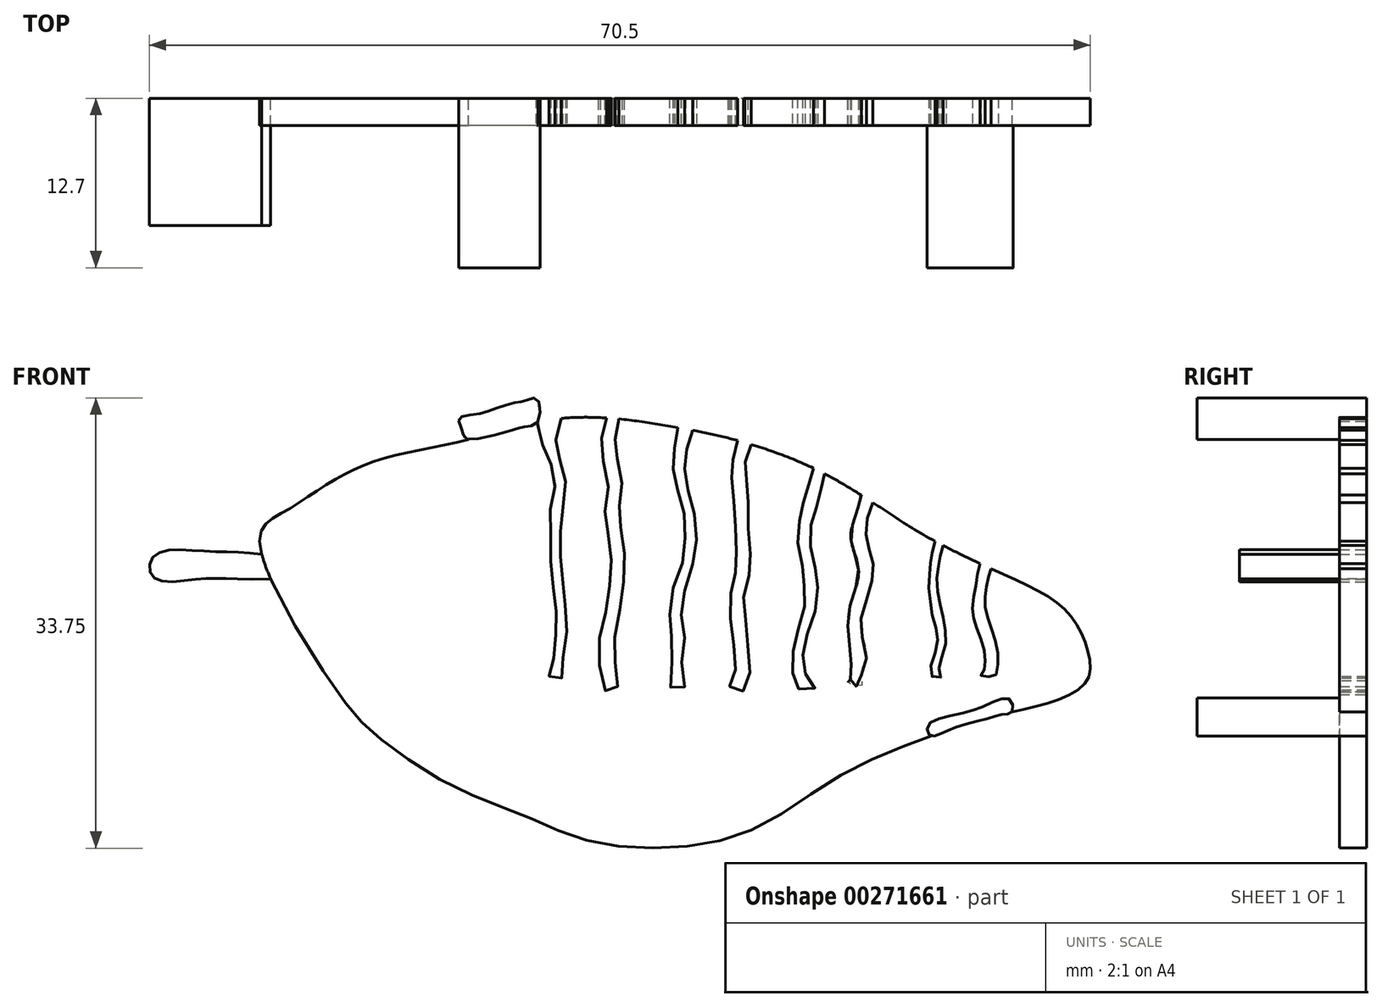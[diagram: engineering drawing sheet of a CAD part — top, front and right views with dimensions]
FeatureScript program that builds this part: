
annotation { "Feature Type Name" : "Feature", "Feature Type Description" : "" }
export const myFeature = defineFeature(function(context is Context, id is Id, definition is map)
    precondition{}
    {
        {
            var Q0;
            Q0=qCreatedBy(makeId("Front.planeOp"),FACE);
            var sketch = newSketch(context, id + "F0", { "sketchPlane" : qUnion([Q0])});
            skFitSpline(sketch, "E0", {"points": [v(-28.45, 9.74) * mm, v(-24.57, 11.38) * mm, v(-19.05, 12.59) * mm, v(-14.06, 13.95) * mm, v(-8.84, 14.4) * mm, v(-3.18, 13.72) * mm, v(2.04, 12.59) * mm, v(7.03, 10.77) * mm, v(11.11, 8.5) * mm, v(16.03, 5.4) * mm, v(22.22, 2.38) * mm, v(26.26, 0) * mm, v(27.9, -2.83) * mm, v(27.9, -5.33) * mm, v(24.5, -7.15) * mm, v(19.73, -8.28) * mm, v(15.38, -9.8) * mm, v(9.52, -12.36) * mm, v(3.4, -16.22) * mm, v(-2.72, -17.8) * mm, v(-9.3, -17.35) * mm, v(-14.06, -15.53) * mm, v(-19.96, -13.04) * mm, v(-25.63, -9.18) * mm, v(-28.34, -6.02) * mm, v(-34.06, 5.34) * mm, v(-32.06, 7.44) * mm, v(-28.45, 9.74) * mm]});
            skFitSpline(sketch, "E1", {"points": [v(-33.9, 4.15) * mm, v(-38.31, 4.39) * mm, v(-41.98, 4.03) * mm, v(-42.01, 2.4) * mm, v(-38.5, 2.3) * mm, v(-33.24, 2.3) * mm], "startDerivative": vector(-21.58, 2.71) * mm, "endDerivative": vector(36.33, 1.24) * mm});
            skSolve(sketch);
        }
        {
            var Q0;
            Q0=makeQuery(id+"F0.imprint","IMPRINT",FACE,{"disambiguationData":[TD([[makeQuery(id+"F0.imprint","IMPRINT",EDGE,{"derivedFrom":sQuery(id+"F0.wireOp",EDGE,"E0")}),-1.0]])]});
            extrude(context, id + "F1", {"entities" : qUnion([Q0]), "depth" : 2.03 * mm});
        }
        {
            var Q0;
            Q0=makeQuery(id+"F1.opExtrude","CAP_FACE",FACE,{"disambiguationData":[OSD([sQuery(id+"F0.wireOp",EDGE,"E0")])],"isStart":false});
            var sketch = newSketch(context, id + "F2", { "sketchPlane" : qUnion([Q0])});
            skSolve(sketch);
        }
        {
            var Q0;
            {var subQ0=sQuery(id+"F0.wireOp",EDGE,"E1");Q0=makeQuery(id+"F0.imprint","IMPRINT",FACE,{"disambiguationData":[TD([[makeQuery(id+"F0.imprint","IMPRINT",EDGE,{"derivedFrom":subQ0}),1.0]])]});}
            extrude(context, id + "F3", {"entities" : qUnion([Q0]), "operationType" : NewBodyOperationType.ADD, "depth" : 9.52 * mm});
        }
        {
            var Q0;
            Q0=qCreatedBy(makeId("Front.planeOp"),FACE);
            var sketch = newSketch(context, id + "F4", { "sketchPlane" : qUnion([Q0])});
            skFitSpline(sketch, "E2", {"points": [v(-13.25, 14.05) * mm, v(-14.17, 13.72) * mm, v(-14.97, 13.51) * mm, v(-18.6, 12.79) * mm, v(-18.88, 13.42) * mm, v(-19.13, 14.32) * mm, v(-17.83, 14.64) * mm, v(-16.4, 15.06) * mm, v(-14.82, 15.53) * mm, v(-14.13, 15.67) * mm, v(-13.29, 15.8) * mm, v(-13.25, 14.05) * mm]});
            skFitSpline(sketch, "E3", {"points": [v(22.33, -7.64) * mm, v(22.1, -6.7) * mm, v(20.53, -7.09) * mm, v(18.1, -7.87) * mm, v(16, -8.65) * mm, v(16.15, -9.44) * mm, v(17, -9.3) * mm, v(18.34, -8.73) * mm, v(20.75, -8.1) * mm, v(21.67, -7.85) * mm, v(22.33, -7.64) * mm]});
            skSolve(sketch);
        }
        {
            var Q0;
            Q0=makeQuery(id+"F4.imprint","IMPRINT",FACE,{"disambiguationData":[TD([[makeQuery(id+"F4.imprint","IMPRINT",EDGE,{"derivedFrom":sQuery(id+"F4.wireOp",EDGE,"E2")}),-1.0]])]});
            var Q1;
            Q1=makeQuery(id+"F4.imprint","IMPRINT",FACE,{"disambiguationData":[TD([[makeQuery(id+"F4.imprint","IMPRINT",EDGE,{"derivedFrom":sQuery(id+"F4.wireOp",EDGE,"E3")}),1.0]])]});
            extrude(context, id + "F5", {"entities" : qUnion([Q0, Q1]), "operationType" : NewBodyOperationType.ADD, "depth" : 12.7 * mm});
        }
        {
            var Q0;
            Q0=makeQuery(id+"F1.opExtrude","CAP_FACE",FACE,{"disambiguationData":[OSD([sQuery(id+"F0.wireOp",EDGE,"E0")])],"isStart":false});
            var sketch = newSketch(context, id + "F6", { "sketchPlane" : qUnion([Q0])});
            skFitSpline(sketch, "E4", {"points": [v(-13.21, 14.11) * mm, v(-12.97, 12.54) * mm, v(-12.35, 11.13) * mm, v(-11.91, 9.55) * mm, v(-12.26, 7.8) * mm, v(-12.26, 5.68) * mm, v(-12.26, 3.4) * mm, v(-12, 1.2) * mm, v(-11.83, -0.65) * mm, v(-11.91, -2.5) * mm, v(-12.18, -4.26) * mm, v(-12.35, -5.05) * mm, v(-11.54, -5.31) * mm, v(-11.46, -4.37) * mm, v(-11.13, -2.67) * mm, v(-11.15, 0) * mm, v(-11.29, 1.38) * mm, v(-11.5, 3.66) * mm, v(-11.55, 5.77) * mm, v(-11.33, 7.75) * mm, v(-11.18, 9.9) * mm, v(-11.7, 11.5) * mm, v(-11.9, 12.7) * mm, v(-11.46, 14.34) * mm, v(-13.21, 14.11) * mm]});
            skFitSpline(sketch, "E5", {"points": [v(-7.17, 14.29) * mm, v(-7.34, 13.33) * mm, v(-7.43, 12.45) * mm, v(-7.34, 11.66) * mm, v(-7.08, 10.52) * mm, v(-6.9, 9.02) * mm, v(-7.08, 7.88) * mm, v(-7.25, 7.09) * mm, v(-6.9, 5.77) * mm, v(-6.73, 4.18) * mm, v(-6.81, 2.34) * mm, v(-6.9, 0.76) * mm, v(-7.43, -1.35) * mm, v(-7.43, -2.59) * mm, v(-7.43, -4.08) * mm, v(-7.25, -5.4) * mm, v(-7.43, -6.28) * mm, v(-8.09, -6.2) * mm, v(-8.52, -4.78) * mm, v(-8.68, -3.37) * mm, v(-8.53, -1.57) * mm, v(-8.09, -0.04) * mm, v(-7.87, 1.54) * mm, v(-7.78, 3.04) * mm, v(-7.74, 4.45) * mm, v(-8.09, 6.25) * mm, v(-8.2, 7.09) * mm, v(-8.09, 8.26) * mm, v(-7.95, 9.72) * mm, v(-8.34, 11.24) * mm, v(-8.5, 12.36) * mm, v(-8.31, 13.66) * mm, v(-8.09, 14.36) * mm, v(-7.17, 14.29) * mm]});
            skFitSpline(sketch, "E6", {"points": [v(-2.74, 13.64) * mm, v(-2.97, 12.63) * mm, v(-3.06, 11.57) * mm, v(-3.08, 10.51) * mm, v(-2.95, 9.72) * mm, v(-2.56, 8.32) * mm, v(-2.24, 6.9) * mm, v(-2.2, 5.42) * mm, v(-2.22, 4) * mm, v(-2.88, 2.47) * mm, v(-3.19, 0.79) * mm, v(-3.36, -0.83) * mm, v(-3.24, -1.89) * mm, v(-3.13, -3.37) * mm, v(-3.37, -5.06) * mm, v(-3.04, -6.12) * mm, v(-2.27, -6) * mm, v(-2.48, -4.78) * mm, v(-2.33, -3.33) * mm, v(-2.24, -1.84) * mm, v(-2.45, -0.64) * mm, v(-2.44, 0.64) * mm, v(-1.92, 2.37) * mm, v(-1.5, 4.02) * mm, v(-1.34, 5.4) * mm, v(-1.47, 7.02) * mm, v(-1.83, 8.43) * mm, v(-2.13, 9.72) * mm, v(-2.22, 10.71) * mm, v(-2.13, 11.69) * mm, v(-1.94, 12.46) * mm, v(-1.62, 13.44) * mm, v(-2.74, 13.64) * mm]});
            skFitSpline(sketch, "E7", {"points": [v(2.76, 12.38) * mm, v(2.39, 11.3) * mm, v(2.3, 10.32) * mm, v(2.48, 9.04) * mm, v(2.52, 7.07) * mm, v(2.61, 4.81) * mm, v(2.72, 3.12) * mm, v(2.28, 1.58) * mm, v(2.24, 0) * mm, v(2.49, -2.02) * mm, v(2.58, -4.28) * mm, v(2.48, -5.97) * mm, v(1.07, -6) * mm, v(1.38, -5.46) * mm, v(1.58, -4.33) * mm, v(1.4, -2.2) * mm, v(1.15, 0) * mm, v(1.38, 1.9) * mm, v(1.62, 3.15) * mm, v(1.64, 4.77) * mm, v(1.54, 6.89) * mm, v(1.4, 8.92) * mm, v(1.28, 10.4) * mm, v(1.4, 11.45) * mm, v(1.74, 12.67) * mm, v(2.76, 12.38) * mm]});
            skFitSpline(sketch, "E8", {"points": [v(7.44, 10.58) * mm, v(7.16, 9.82) * mm, v(6.9, 8.85) * mm, v(6.58, 7.68) * mm, v(6.37, 6.66) * mm, v(6.22, 5.18) * mm, v(6.56, 3.43) * mm, v(6.68, 2.18) * mm, v(6.8, 1.03) * mm, v(6.55, -0.63) * mm, v(6.05, -2.18) * mm, v(5.85, -3.75) * mm, v(5.91, -5.14) * mm, v(6.26, -5.9) * mm, v(7.1, -6.01) * mm, v(7.6, -5.77) * mm, v(6.83, -4.8) * mm, v(6.6, -3.74) * mm, v(6.77, -2.45) * mm, v(7.32, -0.86) * mm, v(7.74, 1.02) * mm, v(7.66, 2.4) * mm, v(7.44, 3.59) * mm, v(7.17, 5.14) * mm, v(7.26, 6.5) * mm, v(7.58, 7.5) * mm, v(7.94, 8.69) * mm, v(8.13, 9.56) * mm, v(8.25, 10.18) * mm, v(7.44, 10.58) * mm]});
            skFitSpline(sketch, "E9", {"points": [v(11.86, 8.02) * mm, v(11.5, 7.01) * mm, v(11.38, 6.03) * mm, v(11.41, 5.04) * mm, v(11.67, 4.33) * mm, v(11.9, 3.32) * mm, v(11.84, 2.34) * mm, v(11.45, 0.88) * mm, v(11, -0.6) * mm, v(11, -1.82) * mm, v(11.41, -3.57) * mm, v(11, -4.7) * mm, v(11, -5.7) * mm, v(10.02, -5.52) * mm, v(10.15, -5.27) * mm, v(10.26, -4.69) * mm, v(10.2, -3.25) * mm, v(10.04, -1.9) * mm, v(10.02, -0.42) * mm, v(10.41, 1.15) * mm, v(10.78, 2.45) * mm, v(10.74, 3.4) * mm, v(10.5, 4.22) * mm, v(10.27, 5.01) * mm, v(10.24, 5.9) * mm, v(10.58, 7.12) * mm, v(10.9, 8.14) * mm, v(11, 8.57) * mm, v(11.47, 8.36) * mm, v(11.86, 8.02) * mm]});
            skFitSpline(sketch, "E10", {"points": [v(16.55, 5.12) * mm, v(16.33, 4.38) * mm, v(16.18, 3.63) * mm, v(16.17, 3.1) * mm, v(16.06, 2.09) * mm, v(16.14, 0.96) * mm, v(16.23, 0) * mm, v(16.5, -1.09) * mm, v(16.69, -1.96) * mm, v(16.66, -2.85) * mm, v(16.3, -3.9) * mm, v(16.2, -4.74) * mm, v(16.49, -5.15) * mm, v(16.96, -5.05) * mm, v(16.84, -4.6) * mm, v(16.88, -4) * mm, v(17.26, -2.98) * mm, v(17.34, -1.98) * mm, v(17.2, -1) * mm, v(16.99, 0) * mm, v(16.78, 0.97) * mm, v(16.67, 2.08) * mm, v(16.73, 2.99) * mm, v(16.84, 3.63) * mm, v(16.97, 4.23) * mm, v(17.13, 4.85) * mm, v(16.82, 5.02) * mm, v(16.55, 5.12) * mm]});
            skFitSpline(sketch, "E11", {"points": [v(20.72, 3.07) * mm, v(20.53, 2.44) * mm, v(20.37, 1.5) * mm, v(20.28, 0.68) * mm, v(20.38, -0.3) * mm, v(20.76, -1.48) * mm, v(21.18, -2.9) * mm, v(21.24, -4.11) * mm, v(21.04, -4.93) * mm, v(20.45, -5.04) * mm, v(19.97, -4.95) * mm, v(20.18, -4.6) * mm, v(20.3, -4.02) * mm, v(20.2, -3) * mm, v(19.82, -1.82) * mm, v(19.46, -0.78) * mm, v(19.34, 0) * mm, v(19.47, 1.28) * mm, v(19.68, 2.29) * mm, v(19.89, 3.45) * mm, v(20.32, 3.25) * mm, v(20.72, 3.07) * mm]});
            skSolve(sketch);
        }
        {
            var Q0;
            {var subQ0=sQuery(id+"F6.wireOp",EDGE,"E5");var subQ1=sQuery(id+"F0.wireOp",EDGE,"E0");var subQ2=makeQuery(id+"F1.opExtrude","SWEPT_FACE",FACE,{"disambiguationData":[OSD([subQ1])]});var subQ3=makeQuery(id+"F1.opExtrude","CAP_FACE",FACE,{"disambiguationData":[OSD([subQ1])],"isStart":false});var subQ4=makeQuery(id+"FEO1aFnhTrQs56K_1.opExtrude","SWEPT_FACE",FACE,{"disambiguationData":[OSD([sQuery(id+"F2.wireOp",EDGE,"58dd70b2-1d15-4010-9a82-05c4c9745bfd")])]});var subQ5=makeQuery(id+"FEO1aFnhTrQs56K_1.boolean.opBoolean","COPY",FACE,{"derivedFrom":subQ4});var subQ6=makeQuery(id+"F5.boolean.opBoolean","SPLIT",EDGE,{"disambiguationData":[TD([subQ5])],"derivedFrom":makeQuery(id+"F3.boolean.opBoolean","SPLIT",EDGE,{"disambiguationData":[TD([subQ2,subQ3,subQ5,makeQuery(id+"F3.opExtrude","SWEPT_FACE",FACE,{"disambiguationData":[OSD([subQ1])]}),makeQuery(id+"F3.opExtrude","SWEPT_FACE",FACE,{"disambiguationData":[OSD([sQuery(id+"F0.wireOp",EDGE,"E1")])]})])],"derivedFrom":makeQuery(id+"FEO1aFnhTrQs56K_1.boolean.opBoolean","SPLIT",EDGE,{"disambiguationData":[TD([subQ2,subQ3,subQ4,makeQuery(id+"FEO1aFnhTrQs56K_1.opExtrude","SWEPT_FACE",FACE,{"disambiguationData":[OSD([sQuery(id+"F2.wireOp",EDGE,"c8b85a6c-cabf-4dfb-9f84-1d43b1ba4017")])]})])],"derivedFrom":makeQuery(id+"F1.opExtrude","CAP_EDGE",EDGE,{"disambiguationData":[OSD([subQ1])],"isStart":false})})})});var subQ7=makeQuery(id+"F6.imprint","INTERSECT",VERTEX,{"disambiguationData":[OD(0.0)],"derivedFrom":[subQ6,subQ0]});Q0=makeQuery(id+"F6.imprint","IMPRINT",FACE,{"disambiguationData":[TD([[makeQuery(id+"F6.imprint","IMPRINT",EDGE,{"disambiguationData":[TD([[subQ7,-1.0]])],"derivedFrom":subQ0}),-1.0]])]});}
            var Q1;
            {var subQ0=sQuery(id+"F6.wireOp",EDGE,"E4");var subQ1=makeQuery(id+"F5.opExtrude","SWEPT_FACE",FACE,{"disambiguationData":[OSD([sQuery(id+"F4.wireOp",EDGE,"E2")])]});var subQ2=sQuery(id+"F0.wireOp",EDGE,"E0");var subQ3=makeQuery(id+"F1.opExtrude","CAP_FACE",FACE,{"disambiguationData":[OSD([subQ2])],"isStart":false});var subQ4=makeQuery(id+"F5.boolean.opBoolean","INTERSECT",EDGE,{"derivedFrom":[subQ3,subQ1]});var subQ5=makeQuery(id+"F6.imprint","INTERSECT",VERTEX,{"derivedFrom":[subQ4,subQ0]});Q1=makeQuery(id+"F6.imprint","IMPRINT",FACE,{"disambiguationData":[TD([[makeQuery(id+"F6.imprint","IMPRINT",EDGE,{"disambiguationData":[TD([[subQ5,-1.0]])],"derivedFrom":subQ0}),1.0]])]});}
            var Q2;
            {var subQ0=sQuery(id+"F6.wireOp",EDGE,"E4");var subQ1=makeQuery(id+"F5.opExtrude","SWEPT_FACE",FACE,{"disambiguationData":[OSD([sQuery(id+"F4.wireOp",EDGE,"E2")])]});var subQ2=sQuery(id+"F0.wireOp",EDGE,"E0");var subQ3=makeQuery(id+"F1.opExtrude","CAP_FACE",FACE,{"disambiguationData":[OSD([subQ2])],"isStart":false});var subQ4=makeQuery(id+"F5.boolean.opBoolean","INTERSECT",EDGE,{"derivedFrom":[subQ3,subQ1]});var subQ5=makeQuery(id+"F6.imprint","INTERSECT",VERTEX,{"disambiguationData":[OD(0.0)],"derivedFrom":[subQ4,subQ0]});Q2=makeQuery(id+"F6.imprint","IMPRINT",FACE,{"disambiguationData":[TD([[makeQuery(id+"F6.imprint","IMPRINT",EDGE,{"disambiguationData":[TD([[subQ5,-1.0]])],"derivedFrom":subQ4}),-1.0]])]});}
            var Q3;
            {var subQ0=sQuery(id+"F6.wireOp",EDGE,"E5");var subQ1=sQuery(id+"F0.wireOp",EDGE,"E0");var subQ2=makeQuery(id+"F5.boolean.opBoolean","SPLIT",EDGE,{"disambiguationData":[TD([makeQuery(id+"F1.opExtrude","SWEPT_FACE",FACE,{"disambiguationData":[OSD([subQ1])]}),makeQuery(id+"F1.opExtrude","CAP_FACE",FACE,{"disambiguationData":[OSD([subQ1])],"isStart":false}),makeQuery(id+"F5.opExtrude","SWEPT_FACE",FACE,{"disambiguationData":[OSD([sQuery(id+"F4.wireOp",EDGE,"E2")])]}),makeQuery(id+"F5.opExtrude","SWEPT_FACE",FACE,{"disambiguationData":[OSD([sQuery(id+"F4.wireOp",EDGE,"E3")])]})])],"derivedFrom":makeQuery(id+"F3.boolean.opBoolean","SPLIT",EDGE,{"disambiguationData":[OD(0.0)],"derivedFrom":makeQuery(id+"F1.opExtrude","CAP_EDGE",EDGE,{"disambiguationData":[OSD([subQ1])],"isStart":false})})});var subQ3=makeQuery(id+"F6.imprint","INTERSECT",VERTEX,{"disambiguationData":[OD(0.0)],"derivedFrom":[subQ2,subQ0]});Q3=makeQuery(id+"F6.imprint","IMPRINT",FACE,{"disambiguationData":[TD([[makeQuery(id+"F6.imprint","IMPRINT",EDGE,{"disambiguationData":[TD([[subQ3,1.0]])],"derivedFrom":subQ0}),-1.0]])]});}
            var Q4;
            {var subQ0=sQuery(id+"F6.wireOp",EDGE,"E6");var subQ1=sQuery(id+"F0.wireOp",EDGE,"E0");var subQ2=makeQuery(id+"F5.boolean.opBoolean","SPLIT",EDGE,{"disambiguationData":[TD([makeQuery(id+"F1.opExtrude","SWEPT_FACE",FACE,{"disambiguationData":[OSD([subQ1])]}),makeQuery(id+"F1.opExtrude","CAP_FACE",FACE,{"disambiguationData":[OSD([subQ1])],"isStart":false}),makeQuery(id+"F5.opExtrude","SWEPT_FACE",FACE,{"disambiguationData":[OSD([sQuery(id+"F4.wireOp",EDGE,"E2")])]}),makeQuery(id+"F5.opExtrude","SWEPT_FACE",FACE,{"disambiguationData":[OSD([sQuery(id+"F4.wireOp",EDGE,"E3")])]})])],"derivedFrom":makeQuery(id+"F3.boolean.opBoolean","SPLIT",EDGE,{"disambiguationData":[OD(0.0)],"derivedFrom":makeQuery(id+"F1.opExtrude","CAP_EDGE",EDGE,{"disambiguationData":[OSD([subQ1])],"isStart":false})})});var subQ3=makeQuery(id+"F6.imprint","INTERSECT",VERTEX,{"disambiguationData":[OD(0.0)],"derivedFrom":[subQ2,subQ0]});Q4=makeQuery(id+"F6.imprint","IMPRINT",FACE,{"disambiguationData":[TD([[makeQuery(id+"F6.imprint","IMPRINT",EDGE,{"disambiguationData":[TD([[subQ3,-1.0]])],"derivedFrom":subQ0}),1.0]])]});}
            var Q5;
            {var subQ0=sQuery(id+"F6.wireOp",EDGE,"E7");var subQ1=sQuery(id+"F0.wireOp",EDGE,"E0");var subQ2=makeQuery(id+"F5.boolean.opBoolean","SPLIT",EDGE,{"disambiguationData":[TD([makeQuery(id+"F1.opExtrude","SWEPT_FACE",FACE,{"disambiguationData":[OSD([subQ1])]}),makeQuery(id+"F1.opExtrude","CAP_FACE",FACE,{"disambiguationData":[OSD([subQ1])],"isStart":false}),makeQuery(id+"F5.opExtrude","SWEPT_FACE",FACE,{"disambiguationData":[OSD([sQuery(id+"F4.wireOp",EDGE,"E2")])]}),makeQuery(id+"F5.opExtrude","SWEPT_FACE",FACE,{"disambiguationData":[OSD([sQuery(id+"F4.wireOp",EDGE,"E3")])]})])],"derivedFrom":makeQuery(id+"F3.boolean.opBoolean","SPLIT",EDGE,{"disambiguationData":[OD(0.0)],"derivedFrom":makeQuery(id+"F1.opExtrude","CAP_EDGE",EDGE,{"disambiguationData":[OSD([subQ1])],"isStart":false})})});var subQ3=makeQuery(id+"F6.imprint","INTERSECT",VERTEX,{"disambiguationData":[OD(0.0)],"derivedFrom":[subQ2,subQ0]});Q5=makeQuery(id+"F6.imprint","IMPRINT",FACE,{"disambiguationData":[TD([[makeQuery(id+"F6.imprint","IMPRINT",EDGE,{"disambiguationData":[TD([[subQ3,-1.0]])],"derivedFrom":subQ0}),-1.0]])]});}
            var Q6;
            {var subQ0=sQuery(id+"F6.wireOp",EDGE,"E8");var subQ1=sQuery(id+"F0.wireOp",EDGE,"E0");var subQ2=makeQuery(id+"F5.boolean.opBoolean","SPLIT",EDGE,{"disambiguationData":[TD([makeQuery(id+"F1.opExtrude","SWEPT_FACE",FACE,{"disambiguationData":[OSD([subQ1])]}),makeQuery(id+"F1.opExtrude","CAP_FACE",FACE,{"disambiguationData":[OSD([subQ1])],"isStart":false}),makeQuery(id+"F5.opExtrude","SWEPT_FACE",FACE,{"disambiguationData":[OSD([sQuery(id+"F4.wireOp",EDGE,"E2")])]}),makeQuery(id+"F5.opExtrude","SWEPT_FACE",FACE,{"disambiguationData":[OSD([sQuery(id+"F4.wireOp",EDGE,"E3")])]})])],"derivedFrom":makeQuery(id+"F3.boolean.opBoolean","SPLIT",EDGE,{"disambiguationData":[OD(0.0)],"derivedFrom":makeQuery(id+"F1.opExtrude","CAP_EDGE",EDGE,{"disambiguationData":[OSD([subQ1])],"isStart":false})})});var subQ3=makeQuery(id+"F6.imprint","INTERSECT",VERTEX,{"disambiguationData":[OD(0.0)],"derivedFrom":[subQ2,subQ0]});Q6=makeQuery(id+"F6.imprint","IMPRINT",FACE,{"disambiguationData":[TD([[makeQuery(id+"F6.imprint","IMPRINT",EDGE,{"disambiguationData":[TD([[subQ3,1.0]])],"derivedFrom":subQ0}),1.0]])]});}
            var Q7;
            {var subQ0=sQuery(id+"F6.wireOp",EDGE,"E9");var subQ1=sQuery(id+"F0.wireOp",EDGE,"E0");var subQ2=makeQuery(id+"F5.boolean.opBoolean","SPLIT",EDGE,{"disambiguationData":[TD([makeQuery(id+"F1.opExtrude","SWEPT_FACE",FACE,{"disambiguationData":[OSD([subQ1])]}),makeQuery(id+"F1.opExtrude","CAP_FACE",FACE,{"disambiguationData":[OSD([subQ1])],"isStart":false}),makeQuery(id+"F5.opExtrude","SWEPT_FACE",FACE,{"disambiguationData":[OSD([sQuery(id+"F4.wireOp",EDGE,"E2")])]}),makeQuery(id+"F5.opExtrude","SWEPT_FACE",FACE,{"disambiguationData":[OSD([sQuery(id+"F4.wireOp",EDGE,"E3")])]})])],"derivedFrom":makeQuery(id+"F3.boolean.opBoolean","SPLIT",EDGE,{"disambiguationData":[OD(0.0)],"derivedFrom":makeQuery(id+"F1.opExtrude","CAP_EDGE",EDGE,{"disambiguationData":[OSD([subQ1])],"isStart":false})})});var subQ3=makeQuery(id+"F6.imprint","INTERSECT",VERTEX,{"disambiguationData":[OD(0.0)],"derivedFrom":[subQ2,subQ0]});Q7=makeQuery(id+"F6.imprint","IMPRINT",FACE,{"disambiguationData":[TD([[makeQuery(id+"F6.imprint","IMPRINT",EDGE,{"disambiguationData":[TD([[subQ3,1.0]])],"derivedFrom":subQ0}),-1.0]])]});}
            var Q8;
            {var subQ0=sQuery(id+"F6.wireOp",EDGE,"E10");var subQ1=sQuery(id+"F0.wireOp",EDGE,"E0");var subQ2=makeQuery(id+"F5.boolean.opBoolean","SPLIT",EDGE,{"disambiguationData":[TD([makeQuery(id+"F1.opExtrude","SWEPT_FACE",FACE,{"disambiguationData":[OSD([subQ1])]}),makeQuery(id+"F1.opExtrude","CAP_FACE",FACE,{"disambiguationData":[OSD([subQ1])],"isStart":false}),makeQuery(id+"F5.opExtrude","SWEPT_FACE",FACE,{"disambiguationData":[OSD([sQuery(id+"F4.wireOp",EDGE,"E2")])]}),makeQuery(id+"F5.opExtrude","SWEPT_FACE",FACE,{"disambiguationData":[OSD([sQuery(id+"F4.wireOp",EDGE,"E3")])]})])],"derivedFrom":makeQuery(id+"F3.boolean.opBoolean","SPLIT",EDGE,{"disambiguationData":[OD(0.0)],"derivedFrom":makeQuery(id+"F1.opExtrude","CAP_EDGE",EDGE,{"disambiguationData":[OSD([subQ1])],"isStart":false})})});var subQ3=makeQuery(id+"F6.imprint","INTERSECT",VERTEX,{"disambiguationData":[OD(0.0)],"derivedFrom":[subQ2,subQ0]});Q8=makeQuery(id+"F6.imprint","IMPRINT",FACE,{"disambiguationData":[TD([[makeQuery(id+"F6.imprint","IMPRINT",EDGE,{"disambiguationData":[TD([[subQ3,-1.0]])],"derivedFrom":subQ0}),1.0]])]});}
            var Q9;
            {var subQ0=sQuery(id+"F6.wireOp",EDGE,"E11");var subQ1=sQuery(id+"F0.wireOp",EDGE,"E0");var subQ2=makeQuery(id+"F5.boolean.opBoolean","SPLIT",EDGE,{"disambiguationData":[TD([makeQuery(id+"F1.opExtrude","SWEPT_FACE",FACE,{"disambiguationData":[OSD([subQ1])]}),makeQuery(id+"F1.opExtrude","CAP_FACE",FACE,{"disambiguationData":[OSD([subQ1])],"isStart":false}),makeQuery(id+"F5.opExtrude","SWEPT_FACE",FACE,{"disambiguationData":[OSD([sQuery(id+"F4.wireOp",EDGE,"E2")])]}),makeQuery(id+"F5.opExtrude","SWEPT_FACE",FACE,{"disambiguationData":[OSD([sQuery(id+"F4.wireOp",EDGE,"E3")])]})])],"derivedFrom":makeQuery(id+"F3.boolean.opBoolean","SPLIT",EDGE,{"disambiguationData":[OD(0.0)],"derivedFrom":makeQuery(id+"F1.opExtrude","CAP_EDGE",EDGE,{"disambiguationData":[OSD([subQ1])],"isStart":false})})});var subQ3=makeQuery(id+"F6.imprint","INTERSECT",VERTEX,{"disambiguationData":[OD(0.0)],"derivedFrom":[subQ2,subQ0]});Q9=makeQuery(id+"F6.imprint","IMPRINT",FACE,{"disambiguationData":[TD([[makeQuery(id+"F6.imprint","IMPRINT",EDGE,{"disambiguationData":[TD([[subQ3,-1.0]])],"derivedFrom":subQ0}),-1.0]])]});}
            var Q10;
            {var subQ0=sQuery(id+"F6.wireOp",EDGE,"E7");var subQ1=sQuery(id+"F0.wireOp",EDGE,"E0");var subQ2=makeQuery(id+"F5.boolean.opBoolean","SPLIT",EDGE,{"disambiguationData":[TD([makeQuery(id+"F1.opExtrude","SWEPT_FACE",FACE,{"disambiguationData":[OSD([subQ1])]}),makeQuery(id+"F1.opExtrude","CAP_FACE",FACE,{"disambiguationData":[OSD([subQ1])],"isStart":false}),makeQuery(id+"F5.opExtrude","SWEPT_FACE",FACE,{"disambiguationData":[OSD([sQuery(id+"F4.wireOp",EDGE,"E2")])]}),makeQuery(id+"F5.opExtrude","SWEPT_FACE",FACE,{"disambiguationData":[OSD([sQuery(id+"F4.wireOp",EDGE,"E3")])]})])],"derivedFrom":makeQuery(id+"F3.boolean.opBoolean","SPLIT",EDGE,{"disambiguationData":[OD(0.0)],"derivedFrom":makeQuery(id+"F1.opExtrude","CAP_EDGE",EDGE,{"disambiguationData":[OSD([subQ1])],"isStart":false})})});var subQ3=makeQuery(id+"F6.imprint","INTERSECT",VERTEX,{"disambiguationData":[OD(0.0)],"derivedFrom":[subQ2,subQ0]});Q10=makeQuery(id+"F6.imprint","IMPRINT",FACE,{"disambiguationData":[TD([[makeQuery(id+"F6.imprint","IMPRINT",EDGE,{"disambiguationData":[TD([[subQ3,1.0]])],"derivedFrom":subQ0}),-1.0]])]});}
            var Q11;
            {var subQ0=sQuery(id+"F6.wireOp",EDGE,"E9");var subQ1=sQuery(id+"F0.wireOp",EDGE,"E0");var subQ2=makeQuery(id+"F5.boolean.opBoolean","SPLIT",EDGE,{"disambiguationData":[TD([makeQuery(id+"F1.opExtrude","SWEPT_FACE",FACE,{"disambiguationData":[OSD([subQ1])]}),makeQuery(id+"F1.opExtrude","CAP_FACE",FACE,{"disambiguationData":[OSD([subQ1])],"isStart":false}),makeQuery(id+"F5.opExtrude","SWEPT_FACE",FACE,{"disambiguationData":[OSD([sQuery(id+"F4.wireOp",EDGE,"E2")])]}),makeQuery(id+"F5.opExtrude","SWEPT_FACE",FACE,{"disambiguationData":[OSD([sQuery(id+"F4.wireOp",EDGE,"E3")])]})])],"derivedFrom":makeQuery(id+"F3.boolean.opBoolean","SPLIT",EDGE,{"disambiguationData":[OD(0.0)],"derivedFrom":makeQuery(id+"F1.opExtrude","CAP_EDGE",EDGE,{"disambiguationData":[OSD([subQ1])],"isStart":false})})});var subQ3=makeQuery(id+"F6.imprint","INTERSECT",VERTEX,{"disambiguationData":[OD(0.0)],"derivedFrom":[subQ2,subQ0]});Q11=makeQuery(id+"F6.imprint","IMPRINT",FACE,{"disambiguationData":[TD([[makeQuery(id+"F6.imprint","IMPRINT",EDGE,{"disambiguationData":[TD([[subQ3,-1.0]])],"derivedFrom":subQ0}),-1.0]])]});}
            var Q12;
            {var subQ0=sQuery(id+"F6.wireOp",EDGE,"E10");var subQ1=sQuery(id+"F0.wireOp",EDGE,"E0");var subQ2=makeQuery(id+"F5.boolean.opBoolean","SPLIT",EDGE,{"disambiguationData":[TD([makeQuery(id+"F1.opExtrude","SWEPT_FACE",FACE,{"disambiguationData":[OSD([subQ1])]}),makeQuery(id+"F1.opExtrude","CAP_FACE",FACE,{"disambiguationData":[OSD([subQ1])],"isStart":false}),makeQuery(id+"F5.opExtrude","SWEPT_FACE",FACE,{"disambiguationData":[OSD([sQuery(id+"F4.wireOp",EDGE,"E2")])]}),makeQuery(id+"F5.opExtrude","SWEPT_FACE",FACE,{"disambiguationData":[OSD([sQuery(id+"F4.wireOp",EDGE,"E3")])]})])],"derivedFrom":makeQuery(id+"F3.boolean.opBoolean","SPLIT",EDGE,{"disambiguationData":[OD(0.0)],"derivedFrom":makeQuery(id+"F1.opExtrude","CAP_EDGE",EDGE,{"disambiguationData":[OSD([subQ1])],"isStart":false})})});var subQ3=makeQuery(id+"F6.imprint","INTERSECT",VERTEX,{"disambiguationData":[OD(0.0)],"derivedFrom":[subQ2,subQ0]});Q12=makeQuery(id+"F6.imprint","IMPRINT",FACE,{"disambiguationData":[TD([[makeQuery(id+"F6.imprint","IMPRINT",EDGE,{"disambiguationData":[TD([[subQ3,1.0]])],"derivedFrom":subQ0}),1.0]])]});}
            var Q13;
            Q13=sQuery(id+"F6.wireOp",EDGE,"E5");
            var Q14;
            Q14=sQuery(id+"F6.wireOp",EDGE,"E4");
            extrude(context, id + "F7", {"entities" : qUnion([Q0, Q1, Q2, Q3, Q4, Q5, Q6, Q7, Q8, Q9, Q10, Q11, Q12]), "operationType" : NewBodyOperationType.REMOVE, "surfaceEntities" : qUnion([Q13, Q14]), "oppositeDirection" : true, "depth" : 25.4 * mm});
        }
    });
